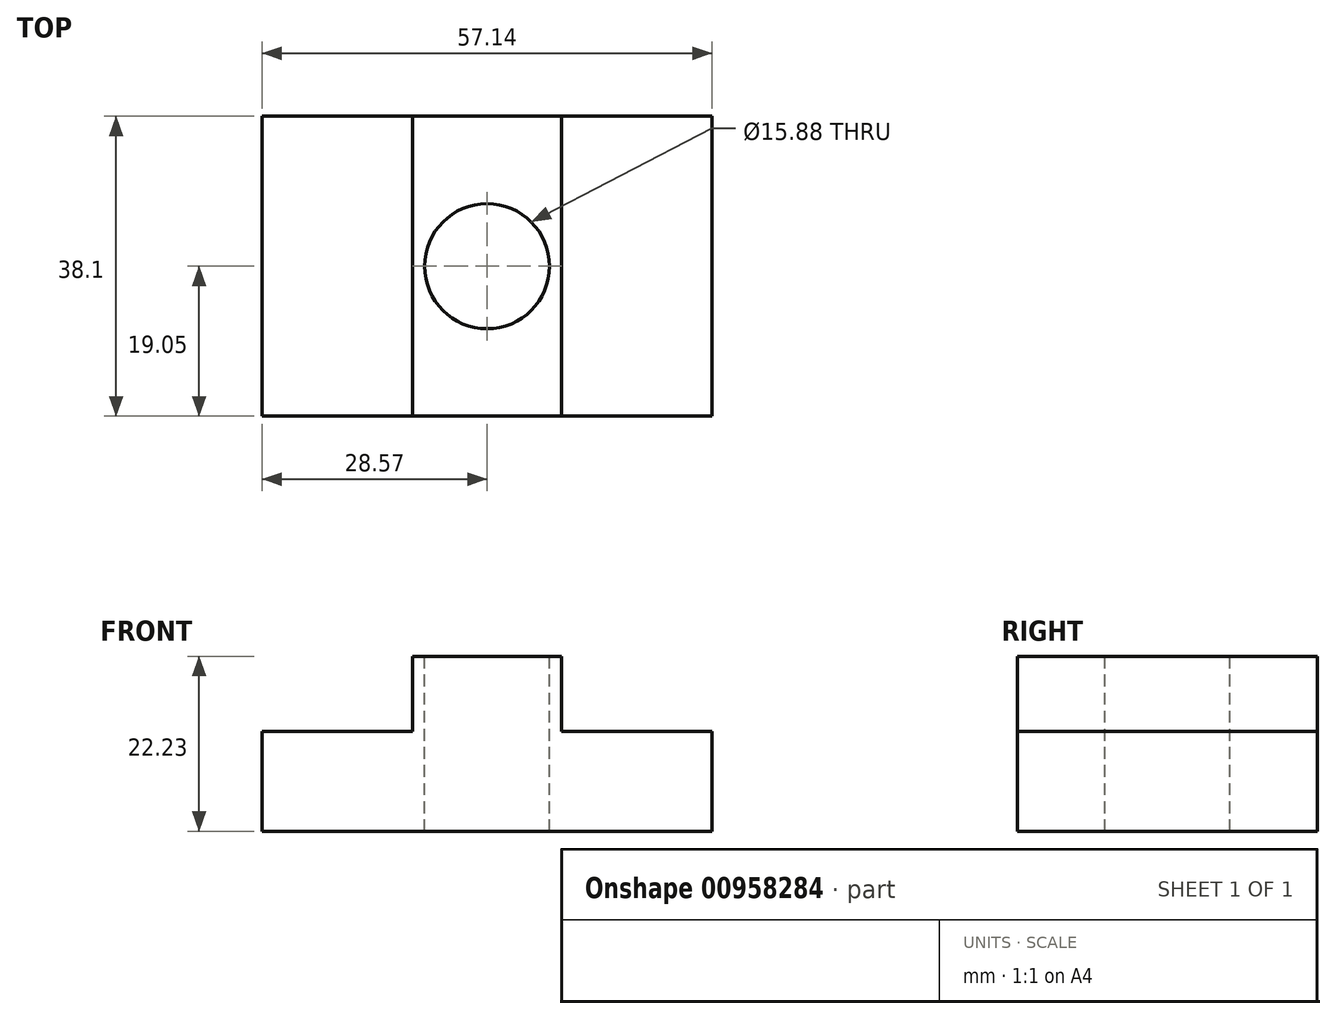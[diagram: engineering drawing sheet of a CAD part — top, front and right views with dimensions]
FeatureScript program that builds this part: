
annotation { "Feature Type Name" : "Feature", "Feature Type Description" : "" }
export const myFeature = defineFeature(function(context is Context, id is Id, definition is map)
    precondition{}
    {
        {
            var Q0;
            Q0=qCreatedBy(makeId("Front.planeOp"),FACE);
            var sketch = newSketch(context, id + "F0", { "sketchPlane" : qUnion([Q0])});
            skLineSegment(sketch, "E0", {"start": v(0, 0) * mm, "end": v(0, 15.19) * mm});
            skLineSegment(sketch, "E1", {"start": v(0, 15.19) * mm, "end": v(9.46, 15.19) * mm});
            skLineSegment(sketch, "E2", {"start": v(9.46, 15.19) * mm, "end": v(9.46, 5.66) * mm});
            skLineSegment(sketch, "E3", {"start": v(9.46, 5.66) * mm, "end": v(28.58, 5.66) * mm});
            skLineSegment(sketch, "E4", {"start": v(28.58, 5.66) * mm, "end": v(28.58, -7.04) * mm});
            skLineSegment(sketch, "E5", {"start": v(28.58, -7.04) * mm, "end": v(0, -7.04) * mm});
            skLineSegment(sketch, "E6", {"start": v(0, -7.04) * mm, "end": v(0, 0) * mm});
            skLineSegment(sketch, "E7.MirrorCS", {"start": v(0, 15.19) * mm, "end": v(-9.46, 15.19) * mm});
            skLineSegment(sketch, "E8.MirrorCS", {"start": v(-9.46, 15.19) * mm, "end": v(-9.46, 5.66) * mm});
            skLineSegment(sketch, "E9.MirrorCS", {"start": v(-9.46, 5.66) * mm, "end": v(-28.58, 5.66) * mm});
            skLineSegment(sketch, "E10.MirrorCS", {"start": v(-28.58, 5.66) * mm, "end": v(-28.58, -7.04) * mm});
            skLineSegment(sketch, "E11.MirrorCS", {"start": v(-28.58, -7.04) * mm, "end": v(0, -7.04) * mm});
            skSolve(sketch);
        }
        {
            var Q0;
            Q0 = qSketchRegion(id + "F0", true);
            extrude(context, id + "F1", {"entities" : qUnion([Q0]), "depth" : 38.1 * mm, "offsetDistance" : 25.4 * mm});
        }
        {
            var Q0;
            Q0=makeQuery(id+"F1.opExtrude","SWEPT_FACE",FACE,{"disambiguationData":[OSD([sQuery(id+"F0.wireOp",EDGE,"E1"),sQuery(id+"F0.wireOp",EDGE,"E7.MirrorCS")])]});
            var sketch = newSketch(context, id + "F2", { "sketchPlane" : qUnion([Q0])});
            skLineSegment(sketch, "E12", {"start": v(0, 0) * mm, "end": v(0, -38.1) * mm});
            skCircle(sketch, "E13", {"center": v(0, -19.05) * mm, "radius": 7.94 * mm});
            skSolve(sketch);
        }
        {
            var Q0;
            Q0=sQuery(id+"F2.wireOp",VERTEX,"E13.center");
            var Q1;
            Q1=makeQuery(id+"F1.opExtrude","SWEPT_BODY",BODY,{"disambiguationData":[OSD([sQuery(id+"F0.wireOp",EDGE,"E1"),sQuery(id+"F0.wireOp",EDGE,"E2"),sQuery(id+"F0.wireOp",EDGE,"E3"),sQuery(id+"F0.wireOp",EDGE,"E4"),sQuery(id+"F0.wireOp",EDGE,"E5"),sQuery(id+"F0.wireOp",EDGE,"E7.MirrorCS"),sQuery(id+"F0.wireOp",EDGE,"E8.MirrorCS"),sQuery(id+"F0.wireOp",EDGE,"E9.MirrorCS"),sQuery(id+"F0.wireOp",EDGE,"E10.MirrorCS"),sQuery(id+"F0.wireOp",EDGE,"E11.MirrorCS")])]});
            hole(context, id + "F3", {"style" : HoleStyle.SIMPLE, "endStyle" : HoleEndStyle.THROUGH, "holeDiameter" : 15.88 * mm, "majorDiameter" : 6.35 * mm, "isTappedThrough" : true, "tappedDepth" : 12.7 * mm, "tapClearance" : 3, "locations" : qUnion([Q0]), "scope" : qUnion([Q1])});
        }
    });
